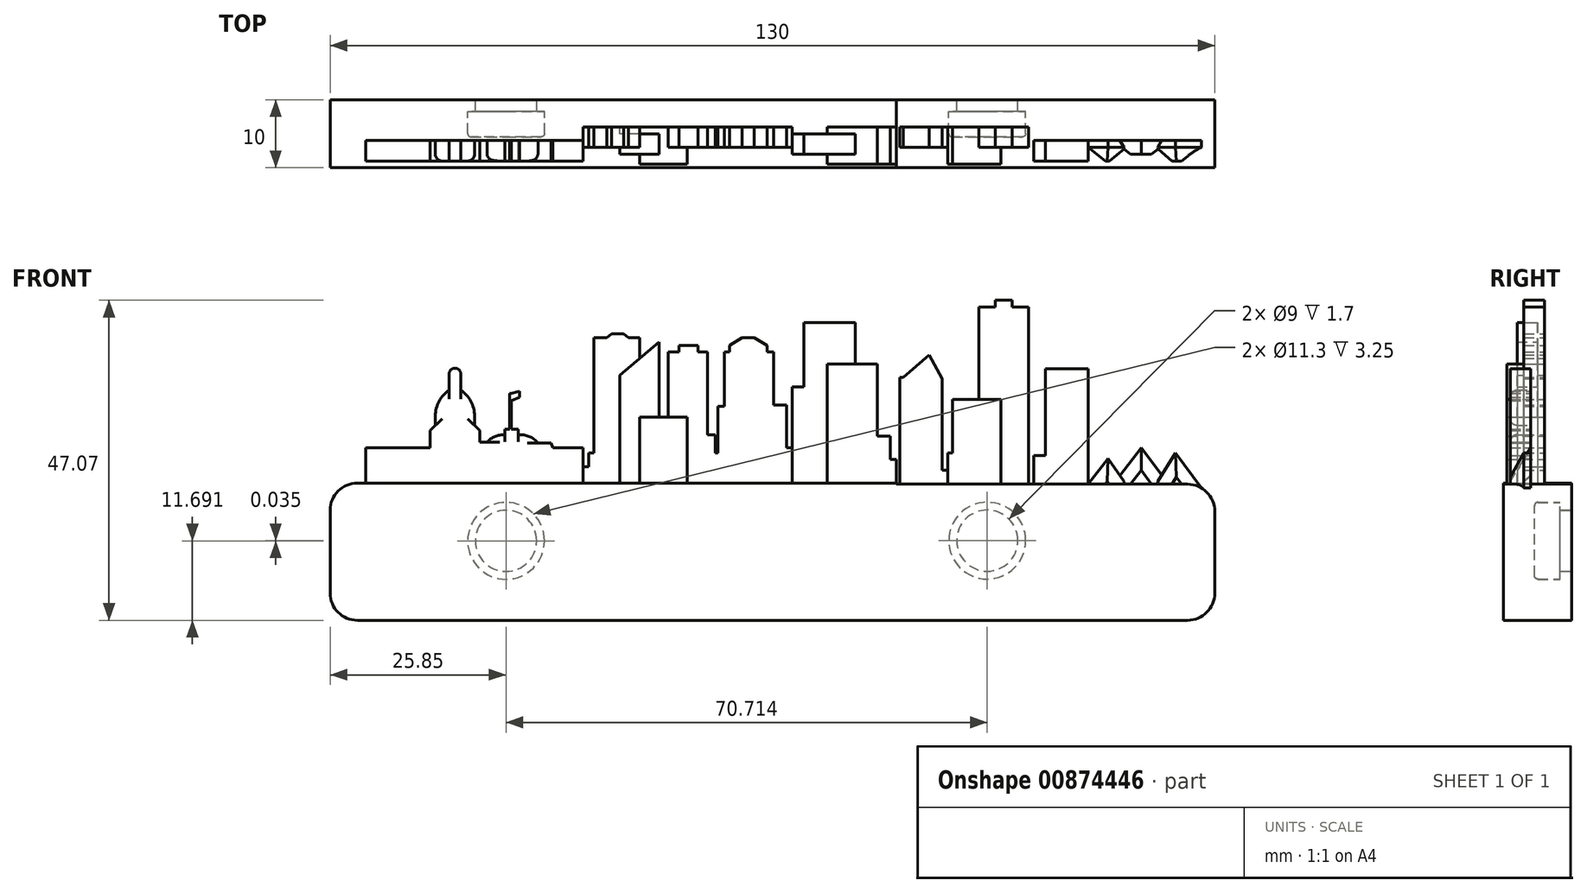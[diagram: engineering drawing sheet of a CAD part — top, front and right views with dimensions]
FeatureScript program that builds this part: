
annotation { "Feature Type Name" : "Feature", "Feature Type Description" : "" }
export const myFeature = defineFeature(function(context is Context, id is Id, definition is map)
    precondition{}
    {
        {
            var Q0;
            Q0=qCreatedBy(makeId("Front.planeOp"),FACE);
            var sketch = newSketch(context, id + "F0", { "sketchPlane" : qUnion([Q0])});
            skLineSegment(sketch, "E0", {"start": v(-70.96, -25.36) * mm, "end": v(59.04, -25.36) * mm});
            skLineSegment(sketch, "E1", {"start": v(59.04, -25.36) * mm, "end": v(59.04, -5.33) * mm});
            skLineSegment(sketch, "E2", {"start": v(59.04, -5.33) * mm, "end": v(56.66, -5.33) * mm});
            skLineSegment(sketch, "E3", {"start": v(56.66, -5.33) * mm, "end": v(53.24, -0.72) * mm});
            skLineSegment(sketch, "E4", {"start": v(53.24, -0.72) * mm, "end": v(51.24, -4) * mm});
            skLineSegment(sketch, "E5", {"start": v(51.24, -4) * mm, "end": v(48.24, 0) * mm});
            skLineSegment(sketch, "E6", {"start": v(48.24, 0) * mm, "end": v(45.1, -4.1) * mm});
            skLineSegment(sketch, "E7", {"start": v(45.1, -4.1) * mm, "end": v(43.33, -1.59) * mm});
            skLineSegment(sketch, "E8", {"start": v(43.33, -1.59) * mm, "end": v(40.44, -5.33) * mm});
            skLineSegment(sketch, "E9", {"start": v(40.44, -5.33) * mm, "end": v(40.44, 11.64) * mm});
            skLineSegment(sketch, "E10", {"start": v(40.44, 11.64) * mm, "end": v(34.13, 11.64) * mm});
            skLineSegment(sketch, "E11", {"start": v(34.13, 11.64) * mm, "end": v(34.13, -1.14) * mm});
            skLineSegment(sketch, "E12", {"start": v(34.13, -1.14) * mm, "end": v(32.42, -1.14) * mm});
            skLineSegment(sketch, "E13", {"start": v(32.42, -1.14) * mm, "end": v(32.42, -5.33) * mm});
            skLineSegment(sketch, "E14", {"start": v(32.42, -5.33) * mm, "end": v(31.67, -5.33) * mm});
            skLineSegment(sketch, "E15", {"start": v(31.67, -5.33) * mm, "end": v(31.67, 20.72) * mm});
            skLineSegment(sketch, "E16", {"start": v(31.67, 20.72) * mm, "end": v(29.25, 20.72) * mm});
            skLineSegment(sketch, "E17", {"start": v(29.25, 20.72) * mm, "end": v(29.25, 21.71) * mm});
            skLineSegment(sketch, "E18", {"start": v(29.25, 21.71) * mm, "end": v(26.78, 21.71) * mm});
            skLineSegment(sketch, "E19", {"start": v(26.78, 21.71) * mm, "end": v(26.78, 20.72) * mm});
            skLineSegment(sketch, "E20", {"start": v(26.78, 20.72) * mm, "end": v(24.35, 20.72) * mm});
            skLineSegment(sketch, "E21", {"start": v(24.35, 20.72) * mm, "end": v(24.35, 7.16) * mm});
            skLineSegment(sketch, "E22", {"start": v(24.35, 7.16) * mm, "end": v(20.5, 7.16) * mm});
            skLineSegment(sketch, "E23", {"start": v(20.5, 7.16) * mm, "end": v(20.5, -0.72) * mm});
            skLineSegment(sketch, "E24", {"start": v(20.5, -0.72) * mm, "end": v(19.79, -0.72) * mm});
            skLineSegment(sketch, "E25", {"start": v(19.79, -0.72) * mm, "end": v(19.79, -3.3) * mm});
            skLineSegment(sketch, "E26", {"start": v(19.79, -3.3) * mm, "end": v(18.98, -3.3) * mm});
            skLineSegment(sketch, "E27", {"start": v(18.98, -3.3) * mm, "end": v(18.98, 10.18) * mm});
            skLineSegment(sketch, "E28", {"start": v(18.98, 10.18) * mm, "end": v(17.07, 13.69) * mm});
            skLineSegment(sketch, "E29", {"start": v(17.07, 13.69) * mm, "end": v(13.28, 10.35) * mm});
            skLineSegment(sketch, "E30", {"start": v(13.28, 10.35) * mm, "end": v(12.77, 10.35) * mm});
            skLineSegment(sketch, "E31", {"start": v(12.77, 10.35) * mm, "end": v(12.77, -5.33) * mm});
            skLineSegment(sketch, "E32", {"start": v(12.77, -5.33) * mm, "end": v(12.24, -5.33) * mm});
            skLineSegment(sketch, "E33", {"start": v(12.24, -5.33) * mm, "end": v(12.24, -1.71) * mm});
            skLineSegment(sketch, "E34", {"start": v(9.43, 1.76) * mm, "end": v(9.43, 12.33) * mm});
            skLineSegment(sketch, "E35", {"start": v(9.43, 12.33) * mm, "end": v(6.18, 12.33) * mm});
            skLineSegment(sketch, "E36", {"start": v(6.18, 12.33) * mm, "end": v(6.18, 18.4) * mm});
            skLineSegment(sketch, "E37", {"start": v(6.18, 18.4) * mm, "end": v(-1.32, 18.4) * mm});
            skLineSegment(sketch, "E38", {"start": v(-1.32, 18.4) * mm, "end": v(-1.32, 9) * mm});
            skLineSegment(sketch, "E39", {"start": v(-1.32, 9) * mm, "end": v(-3.08, 9) * mm});
            skLineSegment(sketch, "E40", {"start": v(-3.08, 9) * mm, "end": v(-3.08, 0) * mm});
            skLineSegment(sketch, "E41", {"start": v(-3.08, 0) * mm, "end": v(-3.85, 0) * mm});
            skLineSegment(sketch, "E42", {"start": v(-3.85, 0) * mm, "end": v(-3.85, 6.33) * mm});
            skLineSegment(sketch, "E43", {"start": v(-3.85, 6.33) * mm, "end": v(-5.81, 6.33) * mm});
            skLineSegment(sketch, "E44", {"start": v(-5.81, 6.33) * mm, "end": v(-5.81, 14.15) * mm});
            skLineSegment(sketch, "E45", {"start": v(-5.81, 14.15) * mm, "end": v(-6.75, 14.15) * mm});
            skLineSegment(sketch, "E46", {"start": v(-6.75, 14.15) * mm, "end": v(-6.75, 15.08) * mm});
            skLineSegment(sketch, "E47", {"start": v(-6.75, 15.08) * mm, "end": v(-8.66, 16.23) * mm});
            skLineSegment(sketch, "E48", {"start": v(-8.66, 16.23) * mm, "end": v(-10.43, 16.23) * mm});
            skLineSegment(sketch, "E49", {"start": v(-10.43, 16.23) * mm, "end": v(-12.24, 15.08) * mm});
            skLineSegment(sketch, "E50", {"start": v(-12.24, 15.08) * mm, "end": v(-12.24, 14.15) * mm});
            skLineSegment(sketch, "E51", {"start": v(-12.24, 14.15) * mm, "end": v(-13.04, 14.15) * mm});
            skLineSegment(sketch, "E52", {"start": v(-13.04, 14.15) * mm, "end": v(-13.04, 6.12) * mm});
            skLineSegment(sketch, "E53", {"start": v(-13.04, 6.12) * mm, "end": v(-14, 6.13) * mm});
            skLineSegment(sketch, "E54", {"start": v(-14, 6.13) * mm, "end": v(-14, -0.72) * mm});
            skLineSegment(sketch, "E55", {"start": v(-14, -0.72) * mm, "end": v(-14.36, -0.72) * mm});
            skLineSegment(sketch, "E56", {"start": v(-14.36, -0.72) * mm, "end": v(-14.36, 1.9) * mm});
            skLineSegment(sketch, "E57", {"start": v(-14.36, 1.9) * mm, "end": v(-15.48, 1.9) * mm});
            skLineSegment(sketch, "E58", {"start": v(-15.48, 1.9) * mm, "end": v(-15.48, 14.15) * mm});
            skLineSegment(sketch, "E59", {"start": v(-15.48, 14.15) * mm, "end": v(-16.9, 14.15) * mm});
            skLineSegment(sketch, "E60", {"start": v(-16.9, 14.15) * mm, "end": v(-16.9, 15.08) * mm});
            skLineSegment(sketch, "E61", {"start": v(-16.9, 15.08) * mm, "end": v(-19.72, 15.08) * mm});
            skLineSegment(sketch, "E62", {"start": v(-19.72, 15.08) * mm, "end": v(-19.72, 14.15) * mm});
            skLineSegment(sketch, "E63", {"start": v(-19.72, 14.15) * mm, "end": v(-21.3, 14.15) * mm});
            skLineSegment(sketch, "E64", {"start": v(-21.3, 14.15) * mm, "end": v(-21.3, 4.51) * mm});
            skLineSegment(sketch, "E65", {"start": v(-21.3, 4.51) * mm, "end": v(-22.63, 4.51) * mm});
            skLineSegment(sketch, "E66", {"start": v(-22.63, 4.51) * mm, "end": v(-22.63, 15.58) * mm});
            skLineSegment(sketch, "E67", {"start": v(-22.63, 15.58) * mm, "end": v(-25.46, 13.18) * mm});
            skLineSegment(sketch, "E68", {"start": v(-25.46, 13.18) * mm, "end": v(-25.46, 16.23) * mm});
            skLineSegment(sketch, "E69", {"start": v(-25.46, 16.23) * mm, "end": v(-27.1, 16.23) * mm});
            skLineSegment(sketch, "E70", {"start": v(-27.1, 16.23) * mm, "end": v(-27.8, 16.8) * mm});
            skLineSegment(sketch, "E71", {"start": v(-27.8, 16.8) * mm, "end": v(-29.6, 16.8) * mm});
            skLineSegment(sketch, "E72", {"start": v(-29.6, 16.8) * mm, "end": v(-30.3, 16.23) * mm});
            skLineSegment(sketch, "E73", {"start": v(-30.3, 16.23) * mm, "end": v(-32.22, 16.23) * mm});
            skLineSegment(sketch, "E74", {"start": v(-32.22, 16.23) * mm, "end": v(-32.22, -0.72) * mm});
            skLineSegment(sketch, "E75", {"start": v(-32.22, -0.72) * mm, "end": v(-32.97, -0.72) * mm});
            skLineSegment(sketch, "E76", {"start": v(-32.97, -0.72) * mm, "end": v(-32.97, -2.75) * mm});
            skLineSegment(sketch, "E77", {"start": v(-33.8, -2.75) * mm, "end": v(-33.8, 0) * mm});
            skLineSegment(sketch, "E78", {"start": v(-33.8, 0) * mm, "end": v(-37.38, 0) * mm});
            skLineSegment(sketch, "E79", {"start": v(-37.38, 0) * mm, "end": v(-38.22, 0) * mm});
            skLineSegment(sketch, "E80", {"start": v(-38.22, 0) * mm, "end": v(-38.5, 0.74) * mm});
            skLineSegment(sketch, "E81", {"start": v(-38.5, 0.74) * mm, "end": v(-40.43, 0.74) * mm});
            skLineSegment(sketch, "E82", {"start": v(-43.3, 1.9) * mm, "end": v(-43.3, 2.76) * mm});
            skLineSegment(sketch, "E83", {"start": v(-43.3, 2.76) * mm, "end": v(-45.31, 2.76) * mm});
            skLineSegment(sketch, "E84", {"start": v(-45.31, 2.76) * mm, "end": v(-45.31, 1.9) * mm});
            skLineSegment(sketch, "E85", {"start": v(-47.9, 0.84) * mm, "end": v(-48.95, 0.84) * mm});
            skLineSegment(sketch, "E86", {"start": v(-48.95, 0.84) * mm, "end": v(-48.95, 2.54) * mm});
            skLineSegment(sketch, "E87", {"start": v(-48.95, 2.54) * mm, "end": v(-49.74, 3.3) * mm});
            skLineSegment(sketch, "E88", {"start": v(-49.74, 3.3) * mm, "end": v(-49.74, 4.72) * mm});
            skLineSegment(sketch, "E89", {"start": v(-51.76, 8.5) * mm, "end": v(-51.76, 10.88) * mm});
            skLineSegment(sketch, "E90", {"start": v(-53.48, 10.88) * mm, "end": v(-53.48, 8.5) * mm});
            skLineSegment(sketch, "E91", {"start": v(-55.5, 4.72) * mm, "end": v(-55.5, 3.3) * mm});
            skLineSegment(sketch, "E92", {"start": v(-55.5, 3.3) * mm, "end": v(-56.3, 2.54) * mm});
            skLineSegment(sketch, "E93", {"start": v(-56.3, 2.54) * mm, "end": v(-56.3, 0) * mm});
            skLineSegment(sketch, "E94", {"start": v(-56.3, 0) * mm, "end": v(-65.71, 0) * mm});
            skLineSegment(sketch, "E95", {"start": v(12.24, -1.71) * mm, "end": v(11.37, -1.71) * mm});
            skLineSegment(sketch, "E96", {"start": v(11.37, -1.71) * mm, "end": v(11.37, 1.76) * mm});
            skLineSegment(sketch, "E97", {"start": v(9.43, 1.76) * mm, "end": v(11.37, 1.76) * mm});
            skArc(sketch, "E98", {"start": v(-45.31, 1.9) * mm, "mid": v(-46.72, 1.67) * mm, "end": v(-47.9, 0.84) * mm});
            skArc(sketch, "E99", {"start": v(-40.43, 0.74) * mm, "mid": v(-41.71, 1.7) * mm, "end": v(-43.3, 1.9) * mm});
            skLineSegment(sketch, "E100", {"start": v(-65.71, -5.18) * mm, "end": v(-70.96, -5.18) * mm});
            skLineSegment(sketch, "E101", {"start": v(-70.96, -5.18) * mm, "end": v(-70.96, -25.36) * mm});
            skLineSegment(sketch, "E102", {"start": v(-65.71, 0) * mm, "end": v(-65.71, -5.18) * mm});
            skArc(sketch, "E103", {"start": v(-51.76, 10.88) * mm, "mid": v(-52.62, 11.74) * mm, "end": v(-53.48, 10.88) * mm});
            skArc(sketch, "E104", {"start": v(-53.48, 8.5) * mm, "mid": v(-54.96, 6.86) * mm, "end": v(-55.5, 4.72) * mm});
            skArc(sketch, "E105", {"start": v(-49.74, 4.72) * mm, "mid": v(-50.28, 6.86) * mm, "end": v(-51.76, 8.5) * mm});
            skLineSegment(sketch, "E106", {"start": v(-44.3, 2.76) * mm, "end": v(-44.3, 8) * mm});
            skLineSegment(sketch, "E107", {"start": v(-44.3, 8) * mm, "end": v(-44.6, 8) * mm});
            skLineSegment(sketch, "E108", {"start": v(-44.6, 8) * mm, "end": v(-44.6, 2.76) * mm});
            skLineSegment(sketch, "E109", {"start": v(-44.3, 8) * mm, "end": v(-43.11, 8.37) * mm});
            skLineSegment(sketch, "E110", {"start": v(-43.11, 8.37) * mm, "end": v(-43.11, 7.47) * mm});
            skLineSegment(sketch, "E111", {"start": v(-33.8, -2.75) * mm, "end": v(-32.97, -2.75) * mm});
            skLineSegment(sketch, "E112", {"start": v(-43.11, 7.47) * mm, "end": v(-44.3, 6.97) * mm});
            skLineSegment(sketch, "E113", {"start": v(-65.71, -5.18) * mm, "end": v(-33.8, -5.18) * mm});
            skLineSegment(sketch, "E114", {"start": v(-33.8, -5.18) * mm, "end": v(-33.8, -2.75) * mm});
            skLineSegment(sketch, "E115", {"start": v(-3.08, 0) * mm, "end": v(-3.08, -5.18) * mm});
            skLineSegment(sketch, "E116", {"start": v(-3.08, -5.18) * mm, "end": v(12.24, -5.18) * mm});
            skLineSegment(sketch, "E117", {"start": v(24.35, 7.16) * mm, "end": v(27.64, 7.16) * mm});
            skLineSegment(sketch, "E118", {"start": v(27.64, 7.16) * mm, "end": v(27.64, -5.33) * mm});
            skLineSegment(sketch, "E119", {"start": v(27.64, -5.33) * mm, "end": v(19.79, -5.33) * mm});
            skLineSegment(sketch, "E120", {"start": v(19.79, -5.33) * mm, "end": v(19.79, -3.3) * mm});
            skLineSegment(sketch, "E121", {"start": v(31.67, -5.33) * mm, "end": v(27.64, -5.33) * mm});
            skLineSegment(sketch, "E122", {"start": v(40.44, -5.33) * mm, "end": v(56.66, -5.33) * mm});
            skLineSegment(sketch, "E123", {"start": v(32.42, -5.33) * mm, "end": v(40.44, -5.33) * mm});
            skLineSegment(sketch, "E124", {"start": v(6.18, 12.33) * mm, "end": v(2.1, 12.33) * mm});
            skLineSegment(sketch, "E125", {"start": v(2.1, 12.33) * mm, "end": v(2.1, -5.18) * mm});
            skLineSegment(sketch, "E126", {"start": v(-25.46, 13.18) * mm, "end": v(-28.38, 10.72) * mm});
            skLineSegment(sketch, "E127", {"start": v(-28.38, 10.72) * mm, "end": v(-28.38, -5.18) * mm});
            skLineSegment(sketch, "E128", {"start": v(-28.38, -5.18) * mm, "end": v(-22.63, -5.18) * mm});
            skLineSegment(sketch, "E129", {"start": v(-22.63, 4.51) * mm, "end": v(-25.46, 4.51) * mm});
            skLineSegment(sketch, "E130", {"start": v(-25.46, 4.51) * mm, "end": v(-25.46, -5.18) * mm});
            skLineSegment(sketch, "E131", {"start": v(-25.46, -5.18) * mm, "end": v(-3.08, -5.18) * mm});
            skLineSegment(sketch, "E132", {"start": v(-21.3, 4.51) * mm, "end": v(-18.48, 4.51) * mm});
            skLineSegment(sketch, "E133", {"start": v(-18.48, 4.51) * mm, "end": v(-18.48, -5.18) * mm});
            skLineSegment(sketch, "E134", {"start": v(-33.8, -5.18) * mm, "end": v(-28.38, -5.18) * mm});
            skLineSegment(sketch, "E135", {"start": v(19.79, -5.33) * mm, "end": v(12.77, -5.33) * mm});
            skLineSegment(sketch, "E136", {"start": v(45.1, -4.1) * mm, "end": v(45.98, -5.33) * mm});
            skLineSegment(sketch, "E137", {"start": v(51.24, -4) * mm, "end": v(50.44, -5.33) * mm});
            skSolve(sketch);
        }
        {
            var Q0;
            Q0=makeQuery(id+"F0.imprint","IMPRINT",FACE,{"disambiguationData":[TD([[makeQuery(id+"F0.imprint","IMPRINT",EDGE,{"derivedFrom":sQuery(id+"F0.wireOp",EDGE,"E0")}),1.0]])]});
            extrude(context, id + "F1", {"entities" : qUnion([Q0]), "depth" : 10 * mm, "offsetDistance" : 25 * mm});
        }
        {
            var Q0;
            Q0=qCreatedBy(makeId("Front.planeOp"),FACE);
            var sketch = newSketch(context, id + "F2", { "sketchPlane" : qUnion([Q0])});
            skCircle(sketch, "E138", {"center": v(-45.1, -13.67) * mm, "radius": 4.5 * mm});
            skCircle(sketch, "E139", {"center": v(-45.1, -13.67) * mm, "radius": 5.65 * mm});
            skCircle(sketch, "E140", {"center": v(-45.1, -13.67) * mm, "radius": 6.85 * mm});
            skCircle(sketch, "E141", {"center": v(25.6, -13.63) * mm, "radius": 4.5 * mm});
            skCircle(sketch, "E142", {"center": v(25.6, -13.63) * mm, "radius": 5.65 * mm});
            skSolve(sketch);
        }
        {
            var Q0;
            Q0=makeQuery(id+"F2.imprint","IMPRINT",FACE,{"disambiguationData":[TD([[makeQuery(id+"F2.imprint","IMPRINT",EDGE,{"derivedFrom":sQuery(id+"F2.wireOp",EDGE,"E138")}),1.0]])]});
            var Q1;
            Q1=makeQuery(id+"F2.imprint","IMPRINT",FACE,{"disambiguationData":[TD([[makeQuery(id+"F2.imprint","IMPRINT",EDGE,{"derivedFrom":sQuery(id+"F2.wireOp",EDGE,"E141")}),1.0]])]});
            extrude(context, id + "F3", {"entities" : qUnion([Q0, Q1]), "operationType" : NewBodyOperationType.REMOVE, "depth" : (3.75 + 1.7) * mm, "offsetDistance" : 25 * mm});
        }
        {
            var Q0;
            Q0=makeQuery(id+"F2.imprint","IMPRINT",FACE,{"disambiguationData":[TD([[makeQuery(id+"F2.imprint","IMPRINT",EDGE,{"derivedFrom":sQuery(id+"F2.wireOp",EDGE,"E138")}),-1.0]])]});
            var Q1;
            Q1=makeQuery(id+"F2.imprint","IMPRINT",FACE,{"disambiguationData":[TD([[makeQuery(id+"F2.imprint","IMPRINT",EDGE,{"derivedFrom":sQuery(id+"F2.wireOp",EDGE,"E141")}),-1.0]])]});
            extrude(context, id + "F4", {"entities" : qUnion([Q0, Q1]), "operationType" : NewBodyOperationType.REMOVE, "depth" : (3.75 + 1.7) * mm, "offsetDistance" : 25 * mm, "hasSecondDirection" : true, "secondDirectionOppositeDirection" : false, "secondDirectionDepth" : 1.7 * mm});
        }
        {
            var Q0;
            Q0=makeQuery(id+"F3.boolean.opBoolean","COPY",EDGE,{"derivedFrom":makeQuery(id+"F3.opExtrude","CAP_EDGE",EDGE,{"disambiguationData":[OSD([sQuery(id+"F2.wireOp",EDGE,"E141")])],"isStart":true})});
            var Q1;
            Q1=makeQuery(id+"F3.boolean.opBoolean","COPY",EDGE,{"derivedFrom":makeQuery(id+"F3.opExtrude","CAP_EDGE",EDGE,{"disambiguationData":[OSD([sQuery(id+"F2.wireOp",EDGE,"E138")])],"isStart":true})});
            var Q2;
            Q2=makeQuery(id+"F4.boolean.opBoolean","COPY",EDGE,{"derivedFrom":makeQuery(id+"F4.opExtrude","CAP_EDGE",EDGE,{"disambiguationData":[OSD([sQuery(id+"F2.wireOp",EDGE,"E141")])],"isStart":true})});
            var Q3;
            Q3=makeQuery(id+"F4.boolean.opBoolean","COPY",EDGE,{"derivedFrom":makeQuery(id+"F4.opExtrude","CAP_EDGE",EDGE,{"disambiguationData":[OSD([sQuery(id+"F2.wireOp",EDGE,"E138")])],"isStart":true})});
            var Q4;
            Q4=makeQuery(id+"F4.boolean.opBoolean","COPY",EDGE,{"derivedFrom":makeQuery(id+"F4.opExtrude","CAP_EDGE",EDGE,{"disambiguationData":[OSD([sQuery(id+"F2.wireOp",EDGE,"E139")])],"isStart":false})});
            var Q5;
            Q5=makeQuery(id+"F4.boolean.opBoolean","COPY",EDGE,{"derivedFrom":makeQuery(id+"F4.opExtrude","CAP_EDGE",EDGE,{"disambiguationData":[OSD([sQuery(id+"F2.wireOp",EDGE,"E142")])],"isStart":false})});
            var Q6;
            Q6=makeQuery(id+"F1.opExtrude","CAP_EDGE",EDGE,{"disambiguationData":[OSD([sQuery(id+"F0.wireOp",EDGE,"E103")])],"isStart":false});
            fillet(context, id + "F5", {"entities" : qUnion([Q0, Q1, Q2, Q3, Q4, Q5, Q6]), "radius" : .5 * mm, "tangentPropagation" : true, "allowEdgeOverflow" : false});
        }
        {
            var Q0;
            Q0=makeQuery(id+"F0.imprint","IMPRINT",FACE,{"disambiguationData":[TD([[makeQuery(id+"F0.imprint","IMPRINT",EDGE,{"derivedFrom":sQuery(id+"F0.wireOp",EDGE,"E77")}),1.0]])]});
            var Q1;
            Q1=makeQuery(id+"F0.imprint","IMPRINT",FACE,{"disambiguationData":[TD([[makeQuery(id+"F0.imprint","IMPRINT",EDGE,{"derivedFrom":sQuery(id+"F0.wireOp",EDGE,"E9")}),1.0]])]});
            var Q2;
            {var subQ0=sQuery(id+"F0.wireOp",EDGE,"E109");Q2=makeQuery(id+"F0.imprint","IMPRINT",FACE,{"disambiguationData":[TD([[makeQuery(id+"F0.imprint","IMPRINT",EDGE,{"derivedFrom":subQ0}),-1.0]])]});}
            var Q3;
            {var subQ0=sQuery(id+"F0.wireOp",EDGE,"E107");Q3=makeQuery(id+"F0.imprint","IMPRINT",FACE,{"disambiguationData":[TD([[makeQuery(id+"F0.imprint","IMPRINT",EDGE,{"derivedFrom":subQ0}),1.0]])]});}
            var Q4;
            Q4=makeQuery(id+"F0.imprint","IMPRINT",FACE,{"disambiguationData":[TD([[makeQuery(id+"F0.imprint","IMPRINT",EDGE,{"derivedFrom":sQuery(id+"F0.wireOp",EDGE,"E3")}),1.0]])]});
            var Q5;
            Q5=makeQuery(id+"F0.imprint","IMPRINT",FACE,{"disambiguationData":[TD([[makeQuery(id+"F0.imprint","IMPRINT",EDGE,{"derivedFrom":sQuery(id+"F0.wireOp",EDGE,"E7")}),1.0]])]});
            extrude(context, id + "F6", {"entities" : qUnion([Q0, Q1, Q2, Q3, Q4, Q5]), "operationType" : NewBodyOperationType.ADD, "depth" : 9 * mm, "offsetDistance" : 25 * mm, "hasSecondDirection" : true, "secondDirectionOppositeDirection" : false, "secondDirectionDepth" : 6 * mm});
        }
        {
            var Q0;
            Q0=makeQuery(id+"F0.imprint","IMPRINT",FACE,{"disambiguationData":[TD([[makeQuery(id+"F0.imprint","IMPRINT",EDGE,{"derivedFrom":sQuery(id+"F0.wireOp",EDGE,"E68")}),1.0]])]});
            var Q1;
            Q1=makeQuery(id+"F0.imprint","IMPRINT",FACE,{"disambiguationData":[TD([[makeQuery(id+"F0.imprint","IMPRINT",EDGE,{"derivedFrom":sQuery(id+"F0.wireOp",EDGE,"E41")}),1.0]])]});
            var Q2;
            Q2=makeQuery(id+"F0.imprint","IMPRINT",FACE,{"disambiguationData":[TD([[makeQuery(id+"F0.imprint","IMPRINT",EDGE,{"derivedFrom":sQuery(id+"F0.wireOp",EDGE,"E15")}),1.0]])]});
            var Q3;
            Q3=makeQuery(id+"F0.imprint","IMPRINT",FACE,{"disambiguationData":[TD([[makeQuery(id+"F0.imprint","IMPRINT",EDGE,{"derivedFrom":sQuery(id+"F0.wireOp",EDGE,"E26")}),1.0]])]});
            extrude(context, id + "F7", {"entities" : qUnion([Q0, Q1, Q2, Q3]), "operationType" : NewBodyOperationType.ADD, "depth" : 7 * mm, "offsetDistance" : 25 * mm, "hasSecondDirection" : true, "secondDirectionOppositeDirection" : false, "secondDirectionDepth" : 4 * mm});
        }
        {
            var Q0;
            Q0=makeQuery(id+"F0.imprint","IMPRINT",FACE,{"disambiguationData":[TD([[makeQuery(id+"F0.imprint","IMPRINT",EDGE,{"derivedFrom":sQuery(id+"F0.wireOp",EDGE,"E66")}),1.0]])]});
            var Q1;
            Q1=makeQuery(id+"F0.imprint","IMPRINT",FACE,{"disambiguationData":[TD([[makeQuery(id+"F0.imprint","IMPRINT",EDGE,{"derivedFrom":sQuery(id+"F0.wireOp",EDGE,"E36")}),1.0]])]});
            extrude(context, id + "F8", {"entities" : qUnion([Q0, Q1]), "operationType" : NewBodyOperationType.ADD, "depth" : 8 * mm, "offsetDistance" : 25 * mm, "hasSecondDirection" : true, "secondDirectionOppositeDirection" : false, "secondDirectionDepth" : 5 * mm});
        }
        {
            var Q0;
            Q0=makeQuery(id+"F0.imprint","IMPRINT",FACE,{"disambiguationData":[TD([[makeQuery(id+"F0.imprint","IMPRINT",EDGE,{"derivedFrom":sQuery(id+"F0.wireOp",EDGE,"E65")}),1.0]])]});
            var Q1;
            Q1=makeQuery(id+"F0.imprint","IMPRINT",FACE,{"disambiguationData":[TD([[makeQuery(id+"F0.imprint","IMPRINT",EDGE,{"derivedFrom":sQuery(id+"F0.wireOp",EDGE,"E22")}),1.0]])]});
            var Q2;
            Q2=makeQuery(id+"F0.imprint","IMPRINT",FACE,{"disambiguationData":[TD([[makeQuery(id+"F0.imprint","IMPRINT",EDGE,{"derivedFrom":sQuery(id+"F0.wireOp",EDGE,"E34")}),1.0]])]});
            extrude(context, id + "F9", {"entities" : qUnion([Q0, Q1, Q2]), "operationType" : NewBodyOperationType.ADD, "depth" : 9.5 * mm, "offsetDistance" : 25 * mm, "hasSecondDirection" : true, "secondDirectionOppositeDirection" : false, "secondDirectionDepth" : 4 * mm});
        }
        {
            var Q0;
            Q0=makeQuery(id+"F0.imprint","IMPRINT",FACE,{"disambiguationData":[TD([[makeQuery(id+"F0.imprint","IMPRINT",EDGE,{"derivedFrom":sQuery(id+"F0.wireOp",EDGE,"E5")}),1.0]])]});
            extrude(context, id + "F10", {"entities" : qUnion([Q0]), "operationType" : NewBodyOperationType.ADD, "depth" : 8 * mm, "offsetDistance" : 25 * mm, "hasSecondDirection" : true, "secondDirectionOppositeDirection" : false, "secondDirectionDepth" : 6 * mm});
        }
        {
            var Q0;
            Q0=makeQuery(id+"F6.opExtrude","CAP_EDGE",EDGE,{"disambiguationData":[OSD([sQuery(id+"F0.wireOp",EDGE,"E98")])],"isStart":false});
            var Q1;
            Q1=makeQuery(id+"F6.opExtrude","CAP_EDGE",EDGE,{"disambiguationData":[OSD([sQuery(id+"F0.wireOp",EDGE,"E99")])],"isStart":false});
            var Q2;
            Q2=makeQuery(id+"F6.opExtrude","CAP_EDGE",EDGE,{"disambiguationData":[OSD([sQuery(id+"F0.wireOp",EDGE,"E105")])],"isStart":false});
            var Q3;
            Q3=makeQuery(id+"F6.opExtrude","CAP_EDGE",EDGE,{"disambiguationData":[OSD([sQuery(id+"F0.wireOp",EDGE,"E104")])],"isStart":false});
            fillet(context, id + "F11", {"entities" : qUnion([Q0, Q1, Q2, Q3]), "radius" : 1 * mm, "tangentPropagation" : true, "allowEdgeOverflow" : false});
        }
        {
            var Q0;
            Q0=makeQuery(id+"F6.opExtrude","CAP_EDGE",EDGE,{"disambiguationData":[OSD([sQuery(id+"F0.wireOp",EDGE,"E7"),sQuery(id+"F0.wireOp",EDGE,"E136")])],"isStart":false});
            var Q1;
            Q1=makeQuery(id+"F6.opExtrude","CAP_EDGE",EDGE,{"disambiguationData":[OSD([sQuery(id+"F0.wireOp",EDGE,"E8")])],"isStart":false});
            var Q2;
            Q2=makeQuery(id+"F10.opExtrude","CAP_EDGE",EDGE,{"disambiguationData":[OSD([sQuery(id+"F0.wireOp",EDGE,"E6")])],"isStart":false});
            var Q3;
            Q3=makeQuery(id+"F10.opExtrude","CAP_EDGE",EDGE,{"disambiguationData":[OSD([sQuery(id+"F0.wireOp",EDGE,"E5")])],"isStart":false});
            var Q4;
            Q4=makeQuery(id+"F6.opExtrude","CAP_EDGE",EDGE,{"disambiguationData":[OSD([sQuery(id+"F0.wireOp",EDGE,"E4"),sQuery(id+"F0.wireOp",EDGE,"E137")])],"isStart":false});
            var Q5;
            Q5=makeQuery(id+"F6.opExtrude","CAP_EDGE",EDGE,{"disambiguationData":[OSD([sQuery(id+"F0.wireOp",EDGE,"E3")])],"isStart":false});
            chamfer(context, id + "F12", {"entities" : qUnion([Q0, Q1, Q2, Q3, Q4, Q5]), "width" : 2 * mm, "tangentPropagation" : true});
        }
        {
            var Q0;
            Q0=makeQuery(id+"F1.opExtrude","SWEPT_EDGE",EDGE,{"disambiguationData":[OSD([sQuery(id+"F0.wireOp",EDGE,"E100"),sQuery(id+"F0.wireOp",EDGE,"E101")])]});
            var Q1;
            Q1=makeQuery(id+"F1.opExtrude","SWEPT_EDGE",EDGE,{"disambiguationData":[OSD([sQuery(id+"F0.wireOp",EDGE,"E0"),sQuery(id+"F0.wireOp",EDGE,"E101")])]});
            var Q2;
            Q2=makeQuery(id+"F1.opExtrude","SWEPT_EDGE",EDGE,{"disambiguationData":[OSD([sQuery(id+"F0.wireOp",EDGE,"E0"),sQuery(id+"F0.wireOp",EDGE,"E1")])]});
            var Q3;
            Q3=makeQuery(id+"F1.opExtrude","SWEPT_EDGE",EDGE,{"disambiguationData":[OSD([sQuery(id+"F0.wireOp",EDGE,"E1"),sQuery(id+"F0.wireOp",EDGE,"E2")])]});
            fillet(context, id + "F13", {"entities" : qUnion([Q0, Q1, Q2, Q3]), "radius" : 4 * mm, "tangentPropagation" : true, "allowEdgeOverflow" : false});
        }
    });
